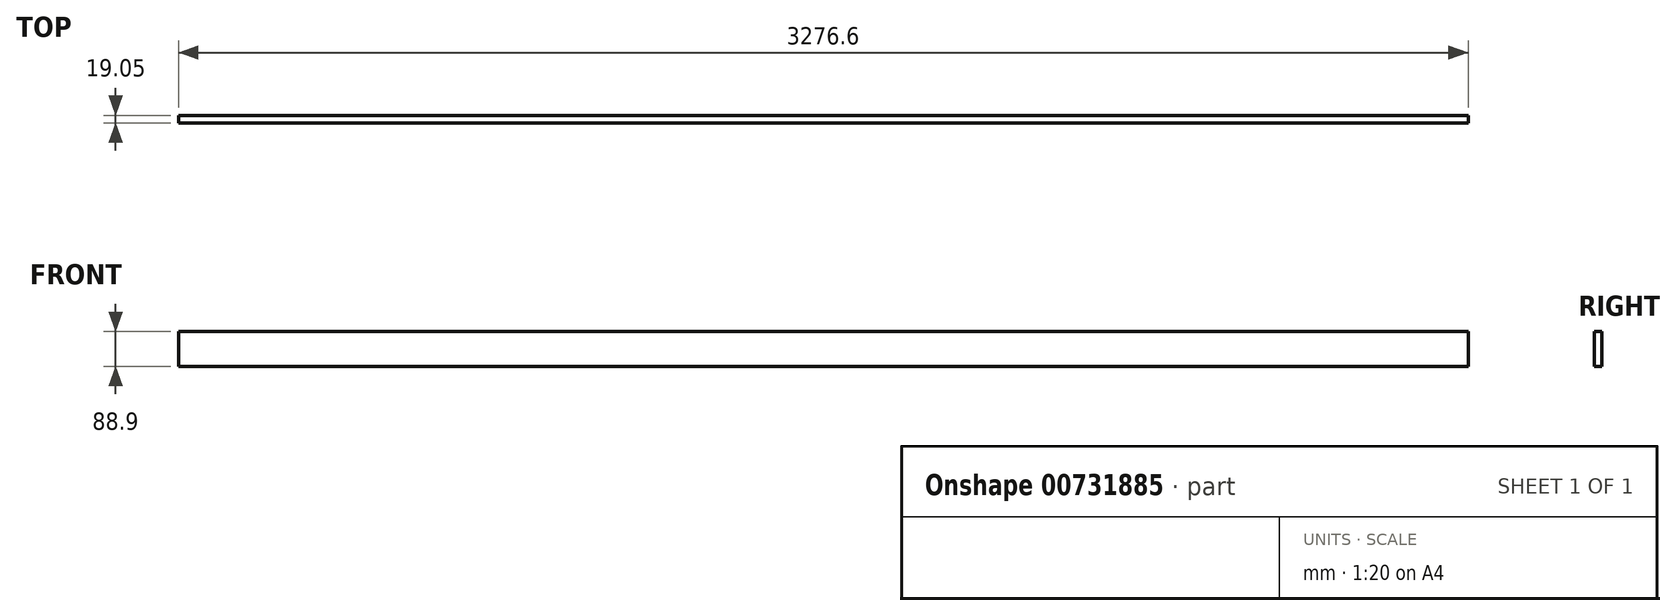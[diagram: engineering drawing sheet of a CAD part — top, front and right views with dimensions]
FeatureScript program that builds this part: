
annotation { "Feature Type Name" : "Feature", "Feature Type Description" : "" }
export const myFeature = defineFeature(function(context is Context, id is Id, definition is map)
    precondition{}
    {
        {
            var Q0;
            Q0=qCreatedBy(makeId("Right.planeOp"),FACE);
            var sketch = newSketch(context, id + "F0", { "sketchPlane" : qUnion([Q0])});
            skLineSegment(sketch, "E0.bottom", {"start": v(0, 0) * mm, "end": v(19.05, 0) * mm});
            skLineSegment(sketch, "E0.top", {"start": v(0, 88.9) * mm, "end": v(19.05, 88.9) * mm});
            skLineSegment(sketch, "E0.left", {"start": v(0, 0) * mm, "end": v(0, 88.9) * mm});
            skLineSegment(sketch, "E0.right", {"start": v(19.05, 0) * mm, "end": v(19.05, 88.9) * mm});
            skSolve(sketch);
        }
        {
            var Q0;
            Q0=makeQuery(id+"F0.imprint","IMPRINT",FACE,{"disambiguationData":[TD([[makeQuery(id+"F0.imprint","IMPRINT",EDGE,{"derivedFrom":sQuery(id+"F0.wireOp",EDGE,"E0.bottom")}),1.0]])]});
            extrude(context, id + "F1", {"entities" : qUnion([Q0]), "depth" : 3276.6 * mm, "offsetDistance" : 25.4 * mm});
        }
    });
